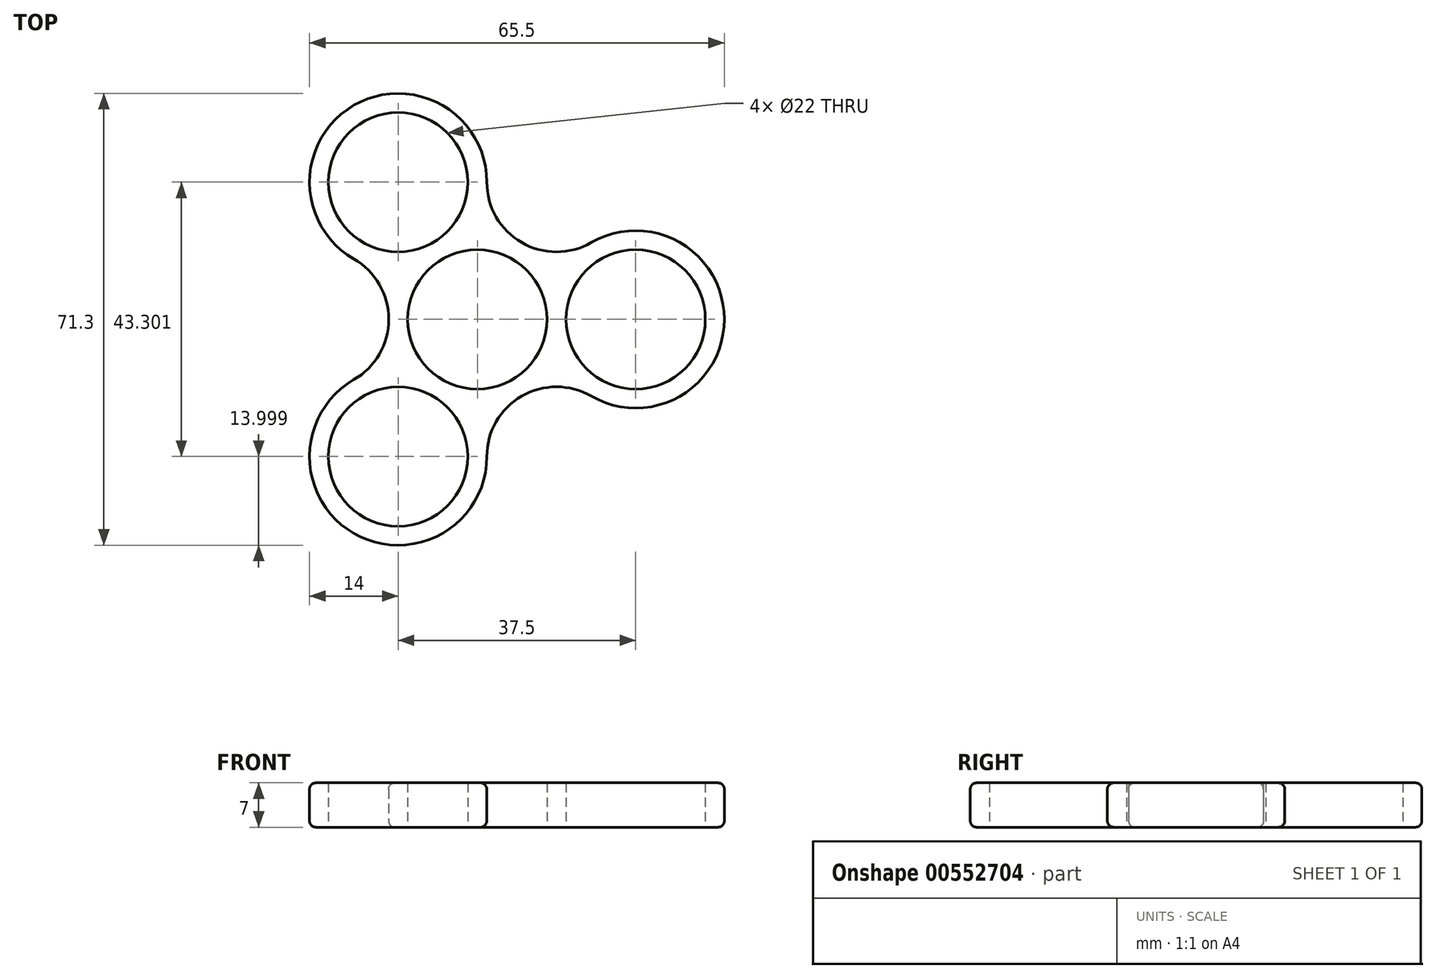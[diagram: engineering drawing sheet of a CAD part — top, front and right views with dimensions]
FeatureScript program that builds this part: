
annotation { "Feature Type Name" : "Feature", "Feature Type Description" : "" }
export const myFeature = defineFeature(function(context is Context, id is Id, definition is map)
    precondition{}
    {
        {
            var Q0;
            Q0=qCreatedBy(makeId("Top.planeOp"),FACE);
            var sketch = newSketch(context, id + "F0", { "sketchPlane" : qUnion([Q0])});
            skCircle(sketch, "E0", {"center": v(0, 0) * mm, "radius": 11 * mm});
            skLineSegment(sketch, "E1", {"start": v(0, 0) * mm, "end": v(25, 0) * mm, "construction": true});
            skCircle(sketch, "E2", {"center": v(25, 0) * mm, "radius": 11 * mm});
            skCircle(sketch, "E3", {"center": v(0, 0) * mm, "radius": 39 * mm, "construction": true});
            skCircle(sketch, "E4", {"center": v(25, 0) * mm, "radius": 14 * mm});
            skLineSegment(sketch, "E5.1.2", {"start": v(0, 0) * mm, "end": v(12.5, 21.65) * mm, "construction": true});
            skCircle(sketch, "E5.2.0", {"center": v(-12.5, 21.65) * mm, "radius": 14 * mm});
            skCircle(sketch, "E5.2.1", {"center": v(-12.5, 21.65) * mm, "radius": 11 * mm});
            skLineSegment(sketch, "E5.2.2", {"start": v(0, 0) * mm, "end": v(-12.5, 21.65) * mm, "construction": true});
            skLineSegment(sketch, "E5.3.2", {"start": v(0, 0) * mm, "end": v(-25, 0) * mm, "construction": true});
            skCircle(sketch, "E5.4.0", {"center": v(-12.5, -21.65) * mm, "radius": 14 * mm});
            skCircle(sketch, "E5.4.1", {"center": v(-12.5, -21.65) * mm, "radius": 11 * mm});
            skLineSegment(sketch, "E5.4.2", {"start": v(0, 0) * mm, "end": v(-12.5, -21.65) * mm, "construction": true});
            skLineSegment(sketch, "E5.5.2", {"start": v(0, 0) * mm, "end": v(12.5, -21.65) * mm, "construction": true});
            skLineSegment(sketch, "E6", {"start": v(25, 0) * mm, "end": v(12.5, 21.65) * mm, "construction": true});
            skLineSegment(sketch, "E7", {"start": v(12.5, 21.65) * mm, "end": v(-12.5, 21.65) * mm, "construction": true});
            skLineSegment(sketch, "E8", {"start": v(-12.5, 21.65) * mm, "end": v(-25, 0) * mm, "construction": true});
            skLineSegment(sketch, "E9", {"start": v(-25, 0) * mm, "end": v(-12.5, -21.65) * mm, "construction": true});
            skLineSegment(sketch, "E10", {"start": v(-12.5, -21.65) * mm, "end": v(1.5, -21.65) * mm, "construction": true});
            skLineSegment(sketch, "E11", {"start": v(12.5, -21.65) * mm, "end": v(18, -12.12) * mm, "construction": true});
            skArc(sketch, "E12", {"start": v(18, 12.12) * mm, "mid": v(18, 31.18) * mm, "end": v(1.5, 21.65) * mm, "construction": true});
            skArc(sketch, "E13", {"start": v(1.5, 21.65) * mm, "mid": v(7, 12.12) * mm, "end": v(18, 12.12) * mm});
            skArc(sketch, "E14", {"start": v(-19.5, -9.53) * mm, "mid": v(-14, 0) * mm, "end": v(-19.5, 9.53) * mm});
            skArc(sketch, "E15", {"start": v(-19.5, 9.53) * mm, "mid": v(-36, 0) * mm, "end": v(-19.5, -9.53) * mm, "construction": true});
            skLineSegment(sketch, "E16", {"start": v(18, -12.12) * mm, "end": v(25, 0) * mm, "construction": true});
            skLineSegment(sketch, "E17", {"start": v(1.5, -21.65) * mm, "end": v(12.5, -21.65) * mm, "construction": true});
            skArc(sketch, "E18", {"start": v(1.5, -21.65) * mm, "mid": v(18, -31.18) * mm, "end": v(18, -12.12) * mm, "construction": true});
            skArc(sketch, "E19", {"start": v(18, -12.12) * mm, "mid": v(7, -12.12) * mm, "end": v(1.5, -21.65) * mm});
            skSolve(sketch);
        }
        {
            var Q0;
            Q0=makeQuery(id+"F0.imprint","IMPRINT",FACE,{"disambiguationData":[TD([[makeQuery(id+"F0.imprint","IMPRINT",EDGE,{"derivedFrom":sQuery(id+"F0.wireOp",EDGE,"E5.4.1")}),-1.0]])]});
            var Q1;
            {var subQ5=sQuery(id+"F0.wireOp",EDGE,"E14");Q1=makeQuery(id+"F0.imprint","IMPRINT",FACE,{"disambiguationData":[TD([[makeQuery(id+"F0.imprint","IMPRINT",EDGE,{"derivedFrom":subQ5}),-1.0]])]});}
            var Q2;
            {var subQ5=sQuery(id+"F0.wireOp",EDGE,"E19");Q2=makeQuery(id+"F0.imprint","IMPRINT",FACE,{"disambiguationData":[TD([[makeQuery(id+"F0.imprint","IMPRINT",EDGE,{"derivedFrom":subQ5}),-1.0]])]});}
            var Q3;
            Q3=makeQuery(id+"F0.imprint","IMPRINT",FACE,{"disambiguationData":[TD([[makeQuery(id+"F0.imprint","IMPRINT",EDGE,{"derivedFrom":sQuery(id+"F0.wireOp",EDGE,"E2")}),-1.0]])]});
            var Q4;
            {var subQ5=sQuery(id+"F0.wireOp",EDGE,"E13");Q4=makeQuery(id+"F0.imprint","IMPRINT",FACE,{"disambiguationData":[TD([[makeQuery(id+"F0.imprint","IMPRINT",EDGE,{"derivedFrom":subQ5}),-1.0]])]});}
            var Q5;
            Q5=makeQuery(id+"F0.imprint","IMPRINT",FACE,{"disambiguationData":[TD([[makeQuery(id+"F0.imprint","IMPRINT",EDGE,{"derivedFrom":sQuery(id+"F0.wireOp",EDGE,"E5.2.1")}),-1.0]])]});
            extrude(context, id + "F1", {"entities" : qUnion([Q0, Q1, Q2, Q3, Q4, Q5]), "depth" : 7 * mm, "offsetDistance" : 25 * mm});
        }
        {
            var Q0;
            Q0=makeQuery(id+"F1.opExtrude","CAP_EDGE",EDGE,{"disambiguationData":[OSD([sQuery(id+"F0.wireOp",EDGE,"E19")])],"isStart":false});
            var Q1;
            Q1=makeQuery(id+"F1.opExtrude","CAP_EDGE",EDGE,{"disambiguationData":[OSD([sQuery(id+"F0.wireOp",EDGE,"E5.4.0")])],"isStart":false});
            var Q2;
            Q2=makeQuery(id+"F1.opExtrude","CAP_EDGE",EDGE,{"disambiguationData":[OSD([sQuery(id+"F0.wireOp",EDGE,"E14")])],"isStart":false});
            var Q3;
            Q3=makeQuery(id+"F1.opExtrude","CAP_EDGE",EDGE,{"disambiguationData":[OSD([sQuery(id+"F0.wireOp",EDGE,"E5.2.0")])],"isStart":false});
            var Q4;
            Q4=makeQuery(id+"F1.opExtrude","CAP_EDGE",EDGE,{"disambiguationData":[OSD([sQuery(id+"F0.wireOp",EDGE,"E13")])],"isStart":false});
            var Q5;
            Q5=makeQuery(id+"F1.opExtrude","CAP_EDGE",EDGE,{"disambiguationData":[OSD([sQuery(id+"F0.wireOp",EDGE,"E4")])],"isStart":false});
            var Q6;
            Q6=makeQuery(id+"F1.opExtrude","CAP_EDGE",EDGE,{"disambiguationData":[OSD([sQuery(id+"F0.wireOp",EDGE,"E19")])],"isStart":true});
            var Q7;
            Q7=makeQuery(id+"F1.opExtrude","CAP_EDGE",EDGE,{"disambiguationData":[OSD([sQuery(id+"F0.wireOp",EDGE,"E5.4.0")])],"isStart":true});
            var Q8;
            Q8=makeQuery(id+"F1.opExtrude","CAP_EDGE",EDGE,{"disambiguationData":[OSD([sQuery(id+"F0.wireOp",EDGE,"E4")])],"isStart":true});
            var Q9;
            Q9=makeQuery(id+"F1.opExtrude","CAP_EDGE",EDGE,{"disambiguationData":[OSD([sQuery(id+"F0.wireOp",EDGE,"E14")])],"isStart":true});
            var Q10;
            Q10=makeQuery(id+"F1.opExtrude","CAP_EDGE",EDGE,{"disambiguationData":[OSD([sQuery(id+"F0.wireOp",EDGE,"E5.2.0")])],"isStart":true});
            var Q11;
            Q11=makeQuery(id+"F1.opExtrude","CAP_EDGE",EDGE,{"disambiguationData":[OSD([sQuery(id+"F0.wireOp",EDGE,"E13")])],"isStart":true});
            fillet(context, id + "F2", {"entities" : qUnion([Q0, Q1, Q2, Q3, Q4, Q5, Q6, Q7, Q8, Q9, Q10, Q11]), "radius" : 1 * mm, "tangentPropagation" : true, "allowEdgeOverflow" : false});
        }
    });
